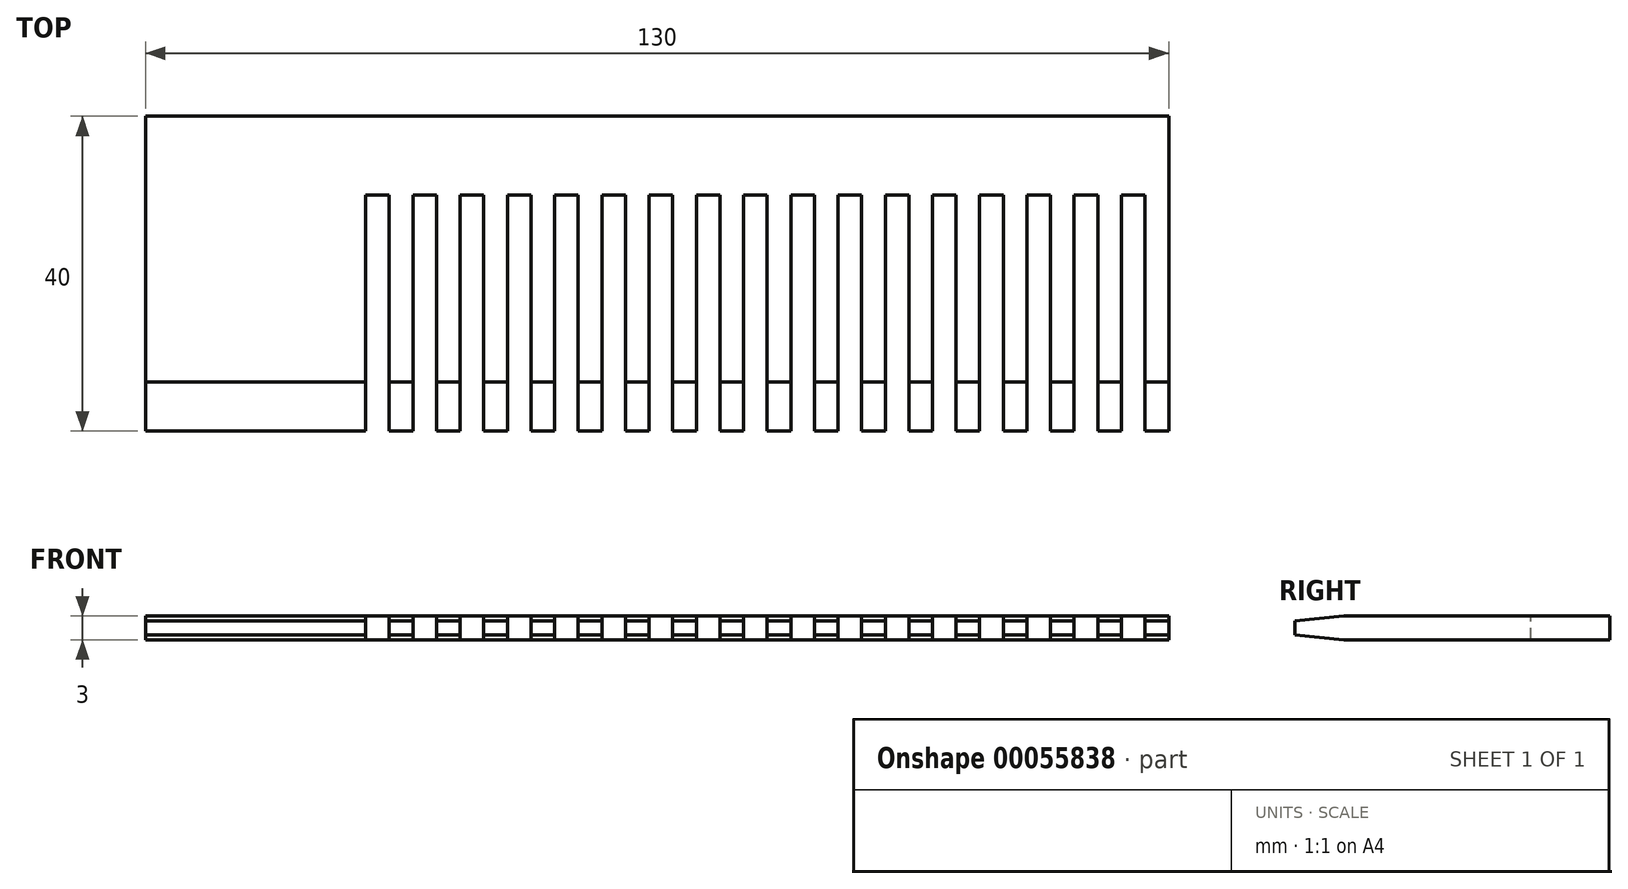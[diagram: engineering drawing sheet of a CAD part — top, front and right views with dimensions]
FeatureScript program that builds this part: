
annotation { "Feature Type Name" : "Feature", "Feature Type Description" : "" }
export const myFeature = defineFeature(function(context is Context, id is Id, definition is map)
    precondition{}
    {
        {
            var Q0;
            Q0=qCreatedBy(makeId("Top.planeOp"),FACE);
            var sketch = newSketch(context, id + "F0", { "sketchPlane" : qUnion([Q0])});
            skLineSegment(sketch, "E0.bottom", {"start": v(-67.75, 51.97) * mm, "end": v(62.25, 51.97) * mm});
            skLineSegment(sketch, "E0.top", {"start": v(-67.75, 11.97) * mm, "end": v(62.25, 11.97) * mm});
            skLineSegment(sketch, "E0.left", {"start": v(-67.75, 51.97) * mm, "end": v(-67.75, 11.97) * mm});
            skLineSegment(sketch, "E0.right", {"start": v(62.25, 51.97) * mm, "end": v(62.25, 11.97) * mm});
            skSolve(sketch);
        }
        {
            var Q0;
            Q0 = qSketchRegion(id + "F0", true);
            extrude(context, id + "F1", {"entities" : qUnion([Q0]), "depth" : 3 * mm});
        }
        {
            var Q0;
            Q0=makeQuery(id+"F1.opExtrude","CAP_FACE",FACE,{"disambiguationData":[OSD([sQuery(id+"F0.wireOp",EDGE,"E0.bottom"),sQuery(id+"F0.wireOp",EDGE,"E0.top"),sQuery(id+"F0.wireOp",EDGE,"E0.left"),sQuery(id+"F0.wireOp",EDGE,"E0.right")])],"isStart":false});
            var sketch = newSketch(context, id + "F2", { "sketchPlane" : qUnion([Q0])});
            skLineSegment(sketch, "E1.bottom", {"start": v(-39.78, 41.97) * mm, "end": v(-36.78, 41.97) * mm});
            skLineSegment(sketch, "E1.top", {"start": v(-39.78, 11.97) * mm, "end": v(-36.78, 11.97) * mm});
            skLineSegment(sketch, "E1.left", {"start": v(-39.78, 41.97) * mm, "end": v(-39.78, 11.97) * mm});
            skLineSegment(sketch, "E1.right", {"start": v(-36.78, 41.97) * mm, "end": v(-36.78, 11.97) * mm});
            skLineSegment(sketch, "E2.1.0.0", {"start": v(-33.78, 41.97) * mm, "end": v(-30.78, 41.97) * mm});
            skLineSegment(sketch, "E2.1.0.1", {"start": v(-33.78, 41.97) * mm, "end": v(-33.78, 11.97) * mm});
            skLineSegment(sketch, "E2.1.0.2", {"start": v(-30.78, 41.97) * mm, "end": v(-30.78, 11.97) * mm});
            skLineSegment(sketch, "E2.1.0.3", {"start": v(-33.78, 11.97) * mm, "end": v(-30.78, 11.97) * mm});
            skLineSegment(sketch, "E2.2.0.0", {"start": v(-27.78, 41.97) * mm, "end": v(-24.78, 41.97) * mm});
            skLineSegment(sketch, "E2.2.0.1", {"start": v(-27.78, 41.97) * mm, "end": v(-27.78, 11.97) * mm});
            skLineSegment(sketch, "E2.2.0.2", {"start": v(-24.78, 41.97) * mm, "end": v(-24.78, 11.97) * mm});
            skLineSegment(sketch, "E2.2.0.3", {"start": v(-27.78, 11.97) * mm, "end": v(-24.78, 11.97) * mm});
            skLineSegment(sketch, "E2.3.0.0", {"start": v(-21.78, 41.97) * mm, "end": v(-18.78, 41.97) * mm});
            skLineSegment(sketch, "E2.3.0.1", {"start": v(-21.78, 41.97) * mm, "end": v(-21.78, 11.97) * mm});
            skLineSegment(sketch, "E2.3.0.2", {"start": v(-18.78, 41.97) * mm, "end": v(-18.78, 11.97) * mm});
            skLineSegment(sketch, "E2.3.0.3", {"start": v(-21.78, 11.97) * mm, "end": v(-18.78, 11.97) * mm});
            skLineSegment(sketch, "E2.4.0.0", {"start": v(-15.78, 41.97) * mm, "end": v(-12.78, 41.97) * mm});
            skLineSegment(sketch, "E2.4.0.1", {"start": v(-15.78, 41.97) * mm, "end": v(-15.78, 11.97) * mm});
            skLineSegment(sketch, "E2.4.0.2", {"start": v(-12.78, 41.97) * mm, "end": v(-12.78, 11.97) * mm});
            skLineSegment(sketch, "E2.4.0.3", {"start": v(-15.78, 11.97) * mm, "end": v(-12.78, 11.97) * mm});
            skLineSegment(sketch, "E2.5.0.0", {"start": v(-9.78, 41.97) * mm, "end": v(-6.78, 41.97) * mm});
            skLineSegment(sketch, "E2.5.0.1", {"start": v(-9.78, 41.97) * mm, "end": v(-9.78, 11.97) * mm});
            skLineSegment(sketch, "E2.5.0.2", {"start": v(-6.78, 41.97) * mm, "end": v(-6.78, 11.97) * mm});
            skLineSegment(sketch, "E2.5.0.3", {"start": v(-9.78, 11.97) * mm, "end": v(-6.78, 11.97) * mm});
            skLineSegment(sketch, "E2.6.0.0", {"start": v(-3.78, 41.97) * mm, "end": v(-0.78, 41.97) * mm});
            skLineSegment(sketch, "E2.6.0.1", {"start": v(-3.78, 41.97) * mm, "end": v(-3.78, 11.97) * mm});
            skLineSegment(sketch, "E2.6.0.2", {"start": v(-0.78, 41.97) * mm, "end": v(-0.78, 11.97) * mm});
            skLineSegment(sketch, "E2.6.0.3", {"start": v(-3.78, 11.97) * mm, "end": v(-0.78, 11.97) * mm});
            skLineSegment(sketch, "E2.7.0.0", {"start": v(2.22, 41.97) * mm, "end": v(5.22, 41.97) * mm});
            skLineSegment(sketch, "E2.7.0.1", {"start": v(2.22, 41.97) * mm, "end": v(2.22, 11.97) * mm});
            skLineSegment(sketch, "E2.7.0.2", {"start": v(5.22, 41.97) * mm, "end": v(5.22, 11.97) * mm});
            skLineSegment(sketch, "E2.7.0.3", {"start": v(2.22, 11.97) * mm, "end": v(5.22, 11.97) * mm});
            skLineSegment(sketch, "E2.8.0.0", {"start": v(8.22, 41.97) * mm, "end": v(11.22, 41.97) * mm});
            skLineSegment(sketch, "E2.8.0.1", {"start": v(8.22, 41.97) * mm, "end": v(8.22, 11.97) * mm});
            skLineSegment(sketch, "E2.8.0.2", {"start": v(11.22, 41.97) * mm, "end": v(11.22, 11.97) * mm});
            skLineSegment(sketch, "E2.8.0.3", {"start": v(8.22, 11.97) * mm, "end": v(11.22, 11.97) * mm});
            skLineSegment(sketch, "E2.9.0.0", {"start": v(14.22, 41.97) * mm, "end": v(17.22, 41.97) * mm});
            skLineSegment(sketch, "E2.9.0.1", {"start": v(14.22, 41.97) * mm, "end": v(14.22, 11.97) * mm});
            skLineSegment(sketch, "E2.9.0.2", {"start": v(17.22, 41.97) * mm, "end": v(17.22, 11.97) * mm});
            skLineSegment(sketch, "E2.9.0.3", {"start": v(14.22, 11.97) * mm, "end": v(17.22, 11.97) * mm});
            skLineSegment(sketch, "E2.10.0.0", {"start": v(20.22, 41.97) * mm, "end": v(23.22, 41.97) * mm});
            skLineSegment(sketch, "E2.10.0.1", {"start": v(20.22, 41.97) * mm, "end": v(20.22, 11.97) * mm});
            skLineSegment(sketch, "E2.10.0.2", {"start": v(23.22, 41.97) * mm, "end": v(23.22, 11.97) * mm});
            skLineSegment(sketch, "E2.10.0.3", {"start": v(20.22, 11.97) * mm, "end": v(23.22, 11.97) * mm});
            skLineSegment(sketch, "E2.11.0.0", {"start": v(26.22, 41.97) * mm, "end": v(29.22, 41.97) * mm});
            skLineSegment(sketch, "E2.11.0.1", {"start": v(26.22, 41.97) * mm, "end": v(26.22, 11.97) * mm});
            skLineSegment(sketch, "E2.11.0.2", {"start": v(29.22, 41.97) * mm, "end": v(29.22, 11.97) * mm});
            skLineSegment(sketch, "E2.11.0.3", {"start": v(26.22, 11.97) * mm, "end": v(29.22, 11.97) * mm});
            skLineSegment(sketch, "E2.12.0.0", {"start": v(32.22, 41.97) * mm, "end": v(35.22, 41.97) * mm});
            skLineSegment(sketch, "E2.12.0.1", {"start": v(32.22, 41.97) * mm, "end": v(32.22, 11.97) * mm});
            skLineSegment(sketch, "E2.12.0.2", {"start": v(35.22, 41.97) * mm, "end": v(35.22, 11.97) * mm});
            skLineSegment(sketch, "E2.12.0.3", {"start": v(32.22, 11.97) * mm, "end": v(35.22, 11.97) * mm});
            skLineSegment(sketch, "E2.13.0.0", {"start": v(38.22, 41.97) * mm, "end": v(41.22, 41.97) * mm});
            skLineSegment(sketch, "E2.13.0.1", {"start": v(38.22, 41.97) * mm, "end": v(38.22, 11.97) * mm});
            skLineSegment(sketch, "E2.13.0.2", {"start": v(41.22, 41.97) * mm, "end": v(41.22, 11.97) * mm});
            skLineSegment(sketch, "E2.13.0.3", {"start": v(38.22, 11.97) * mm, "end": v(41.22, 11.97) * mm});
            skLineSegment(sketch, "E2.14.0.0", {"start": v(44.22, 41.97) * mm, "end": v(47.22, 41.97) * mm});
            skLineSegment(sketch, "E2.14.0.1", {"start": v(44.22, 41.97) * mm, "end": v(44.22, 11.97) * mm});
            skLineSegment(sketch, "E2.14.0.2", {"start": v(47.22, 41.97) * mm, "end": v(47.22, 11.97) * mm});
            skLineSegment(sketch, "E2.14.0.3", {"start": v(44.22, 11.97) * mm, "end": v(47.22, 11.97) * mm});
            skLineSegment(sketch, "E2.15.0.0", {"start": v(50.22, 41.97) * mm, "end": v(53.22, 41.97) * mm});
            skLineSegment(sketch, "E2.15.0.1", {"start": v(50.22, 41.97) * mm, "end": v(50.22, 11.97) * mm});
            skLineSegment(sketch, "E2.15.0.2", {"start": v(53.22, 41.97) * mm, "end": v(53.22, 11.97) * mm});
            skLineSegment(sketch, "E2.15.0.3", {"start": v(50.22, 11.97) * mm, "end": v(53.22, 11.97) * mm});
            skLineSegment(sketch, "E2.16.0.0", {"start": v(56.22, 41.97) * mm, "end": v(59.22, 41.97) * mm});
            skLineSegment(sketch, "E2.16.0.1", {"start": v(56.22, 41.97) * mm, "end": v(56.22, 11.97) * mm});
            skLineSegment(sketch, "E2.16.0.2", {"start": v(59.22, 41.97) * mm, "end": v(59.22, 11.97) * mm});
            skLineSegment(sketch, "E2.16.0.3", {"start": v(56.22, 11.97) * mm, "end": v(59.22, 11.97) * mm});
            skLineSegment(sketch, "E2.direction1", {"start": v(-39.78, 41.97) * mm, "end": v(-33.78, 41.97) * mm, "construction": true});
            skSolve(sketch);
        }
        {
            var Q0;
            Q0 = qSketchRegion(id + "F2", true);
            extrude(context, id + "F3", {"entities" : qUnion([Q0]), "operationType" : NewBodyOperationType.REMOVE, "oppositeDirection" : true, "depth" : 25 * mm});
        }
        {
            var Q0;
            Q0=makeQuery(id+"F1.opExtrude","SWEPT_FACE",FACE,{"disambiguationData":[OSD([sQuery(id+"F0.wireOp",EDGE,"E0.left")])]});
            var sketch = newSketch(context, id + "F4", { "sketchPlane" : qUnion([Q0])});
            skLineSegment(sketch, "E3", {"start": v(-11.97, 2.4) * mm, "end": v(-18.21, 3) * mm});
            skLineSegment(sketch, "E4", {"start": v(-18.21, 3) * mm, "end": v(-11.97, 3) * mm});
            skLineSegment(sketch, "E5", {"start": v(-11.97, 3) * mm, "end": v(-11.97, 2.4) * mm});
            skLineSegment(sketch, "E6", {"start": v(-11.97, 1.5) * mm, "end": v(-19.38, 1.5) * mm, "construction": true});
            skLineSegment(sketch, "E7.MirrorCS", {"start": v(-11.97, 0) * mm, "end": v(-11.97, 0.6) * mm});
            skLineSegment(sketch, "E8.MirrorCS", {"start": v(-18.21, 0) * mm, "end": v(-11.97, 0) * mm});
            skLineSegment(sketch, "E9.MirrorCS", {"start": v(-11.97, 0.6) * mm, "end": v(-18.21, 0) * mm});
            skSolve(sketch);
        }
        {
            var Q0;
            Q0=makeQuery(id+"F4.imprint","IMPRINT",FACE,{"disambiguationData":[TD([[makeQuery(id+"F4.imprint","IMPRINT",EDGE,{"derivedFrom":sQuery(id+"F4.wireOp",EDGE,"E3")}),-1.0]])]});
            var Q1;
            Q1=makeQuery(id+"F4.imprint","IMPRINT",FACE,{"disambiguationData":[TD([[makeQuery(id+"F4.imprint","IMPRINT",EDGE,{"derivedFrom":sQuery(id+"F4.wireOp",EDGE,"E7.MirrorCS")}),-1.0]])]});
            extrude(context, id + "F5", {"entities" : qUnion([Q0, Q1]), "operationType" : NewBodyOperationType.REMOVE, "endBound" : BoundingType.THROUGH_ALL, "oppositeDirection" : true, "depth" : 25 * mm});
        }
    });
